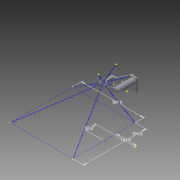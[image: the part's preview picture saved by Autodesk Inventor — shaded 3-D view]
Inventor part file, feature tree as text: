
AUTODESK INVENTOR PART (.ipt)
format: ipt  version: 2014 (Build 180170000, 170)  size: 800,256 bytes
history: native  units: mm
features: sketch x20, extrude x10, fillet x7, plane x4, projected_geometry x3, other x2, hole x1, revolve x1, loft x1
ambient origin geometry x8: Origin, YZ Plane, XZ Plane, XY Plane, X Axis, Y Axis, Z Axis, Center Point
bodies: Solid1 (feature_tree)
feature tree (49):
  extrude  "Extrusion1"  Depth=30.0mm
  hole  "Hole1"  [1 undecoded]
  extrude  "Extrusion2"  Depth=4.0mm
  extrude  "Extrusion10"  Depth=15.0mm
  revolve  "Revolution1"  [1 undecoded]
  extrude  "Extrusion11"  TaperAngle=45.0deg  [1 undecoded]
  extrude  "Extrusion12"  Depth=3.0mm
  fillet  "Fillet7"  [1 undecoded]
  fillet  "Fillet8"  Radius=42.686809mm
  extrude  "Extrusion13"  Depth=22.0mm
  extrude  "Extrusion14"  Depth=10.0mm
  plane  "Work Plane3"
  loft  "Loft1"
  sketch  "Sketch27"  dims[d103=15.0mm d104=0.0mm]
  other  "Work Axis1"
  sketch  "Sketch28"  dims[d105=14.0mm]
  plane  "Work Plane4"
  extrude  "Extrusion16"  Depth=159.5mm
  extrude  "Extrusion17"  Depth=10.0mm
  fillet  "Fillet9"  Radius=10.0mm
  fillet  "Fillet10"  Radius=90.0mm
  fillet  "Fillet11"  Radius=10.0mm
  fillet  "Fillet12"  Radius=10.0mm
  extrude  "Extrusion18"  TaperAngle=0.0deg  [1 undecoded]
  fillet  "Fillet14"  Radius=25.0mm
  plane  "Work Plane5"
  sketch  "Sketch32"  dims[d106=55.0mm d107=0.0mm]
  other  "Work Point1"
  sketch  "Sketch33"  dims[d108=4.0mm]
  plane  "Work Plane6"
  sketch  "Sketch34"  dims[d109=4.0mm d110=2.0mm d111=1.0mm d112=5.75mm d113=0.0mm d114=0.0mm d116=38.1mm d117=111.398138mm d118=32.0mm d119=0.0mm d120=90.0deg d121=0.0mm d122=90.0deg d125=20.0mm d126=6.981317mm d127=1.0mm d135=-254.0mm d136=304.8mm d137=304.8mm d138=101.6mm d139=50.8mm d140=45.0mm d141=180.0mm d142=85.0mm]
  sketch  "3D Sketch3"
  sketch  "Sketch1"  dims[d0=61.0mm d1=30.0mm]
  sketch  "Sketch2"  dims[d2=7.0mm d3=0.0mm d5=20.0mm]
  sketch  "Sketch3"  dims[d6=20.0mm]
  sketch  "Sketch15"  dims[d7=3.25mm d8=6.0mm d9=4.0mm d10=2.0mm d11=90.0deg d12=8.0mm d13=20.594885mm d14=5.5mm]
  sketch  "Sketch16"  dims[d15=2.4mm d16=0.0mm d64=15.0mm]
  projected_geometry  "Projected Loop5"
  sketch  "Sketch17"  dims[d65=30.0mm d66=18.0mm]
  projected_geometry  "Projected Loop6"
  sketch  "Sketch18"  dims[d67=90.0mm d68=0.0mm d69=45.0deg]
  sketch  "Sketch19"  dims[d71=8.0mm d72=3.0mm d73=90.0deg d74=42.686809mm]
  sketch  "Sketch20"  dims[d75=15.0mm d76=22.0mm]
  sketch  "Sketch22"  dims[d77=90.0mm d78=0.0mm d79=10.0mm]
  sketch  "Sketch23"  dims[d80=0.0mm d81=0.0mm d82=2.0mm]
  sketch  "Sketch24"  dims[d83=2.0mm d84=159.5mm]
  sketch  "Sketch25"  dims[d85=12.0mm d86=12.0mm d88=10.0mm d90=90.0mm d91=0.0mm d92=10.0mm d93=10.0mm]
  sketch  "Sketch26"  dims[d94=6.0mm d96=0.0mm d97=0.0mm d102=25.0mm]
  projected_geometry  "Projected Loop7"
note: 5 required parameter values undecoded (feature->parameter linkage not recoverable at this tier; creation-order binding heuristic only, values carry confidence <= 0.55)